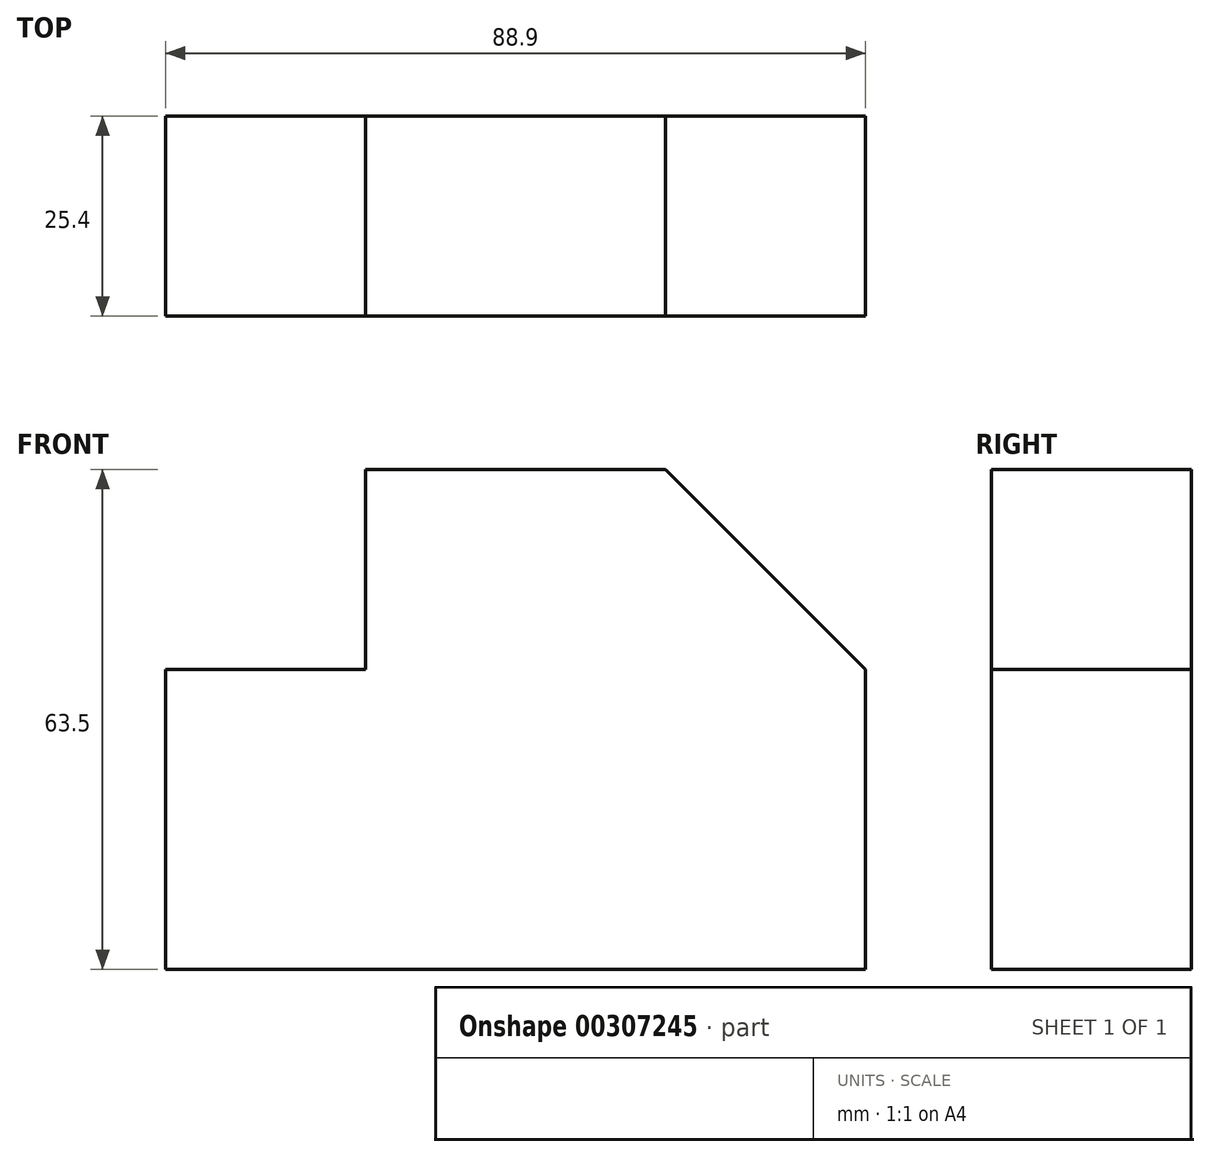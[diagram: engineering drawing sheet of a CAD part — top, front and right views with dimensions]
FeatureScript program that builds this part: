
annotation { "Feature Type Name" : "Feature", "Feature Type Description" : "" }
export const myFeature = defineFeature(function(context is Context, id is Id, definition is map)
    precondition{}
    {
        {
            var Q0;
            Q0=qCreatedBy(makeId("Front.planeOp"),FACE);
            var sketch = newSketch(context, id + "F0", { "sketchPlane" : qUnion([Q0])});
            skLineSegment(sketch, "E0", {"start": v(-43.06, -45.93) * mm, "end": v(-43.06, -7.83) * mm});
            skLineSegment(sketch, "E1", {"start": v(-43.06, -7.83) * mm, "end": v(-17.66, -7.83) * mm});
            skLineSegment(sketch, "E2", {"start": v(-17.66, -7.83) * mm, "end": v(-17.66, 17.57) * mm});
            skLineSegment(sketch, "E3", {"start": v(-17.66, 17.57) * mm, "end": v(20.44, 17.57) * mm});
            skLineSegment(sketch, "E4", {"start": v(20.44, 17.57) * mm, "end": v(45.84, -7.83) * mm});
            skLineSegment(sketch, "E5", {"start": v(45.84, -7.83) * mm, "end": v(45.84, -45.93) * mm});
            skLineSegment(sketch, "E6", {"start": v(45.84, -45.93) * mm, "end": v(-43.06, -45.93) * mm});
            skSolve(sketch);
        }
        {
            var Q0;
            Q0=makeQuery(id+"F0.imprint","IMPRINT",FACE,{"disambiguationData":[TD([[makeQuery(id+"F0.imprint","IMPRINT",EDGE,{"derivedFrom":sQuery(id+"F0.wireOp",EDGE,"E0")}),-1.0]])]});
            extrude(context, id + "F1", {"entities" : qUnion([Q0]), "depth" : 25.4 * mm});
        }
    });
